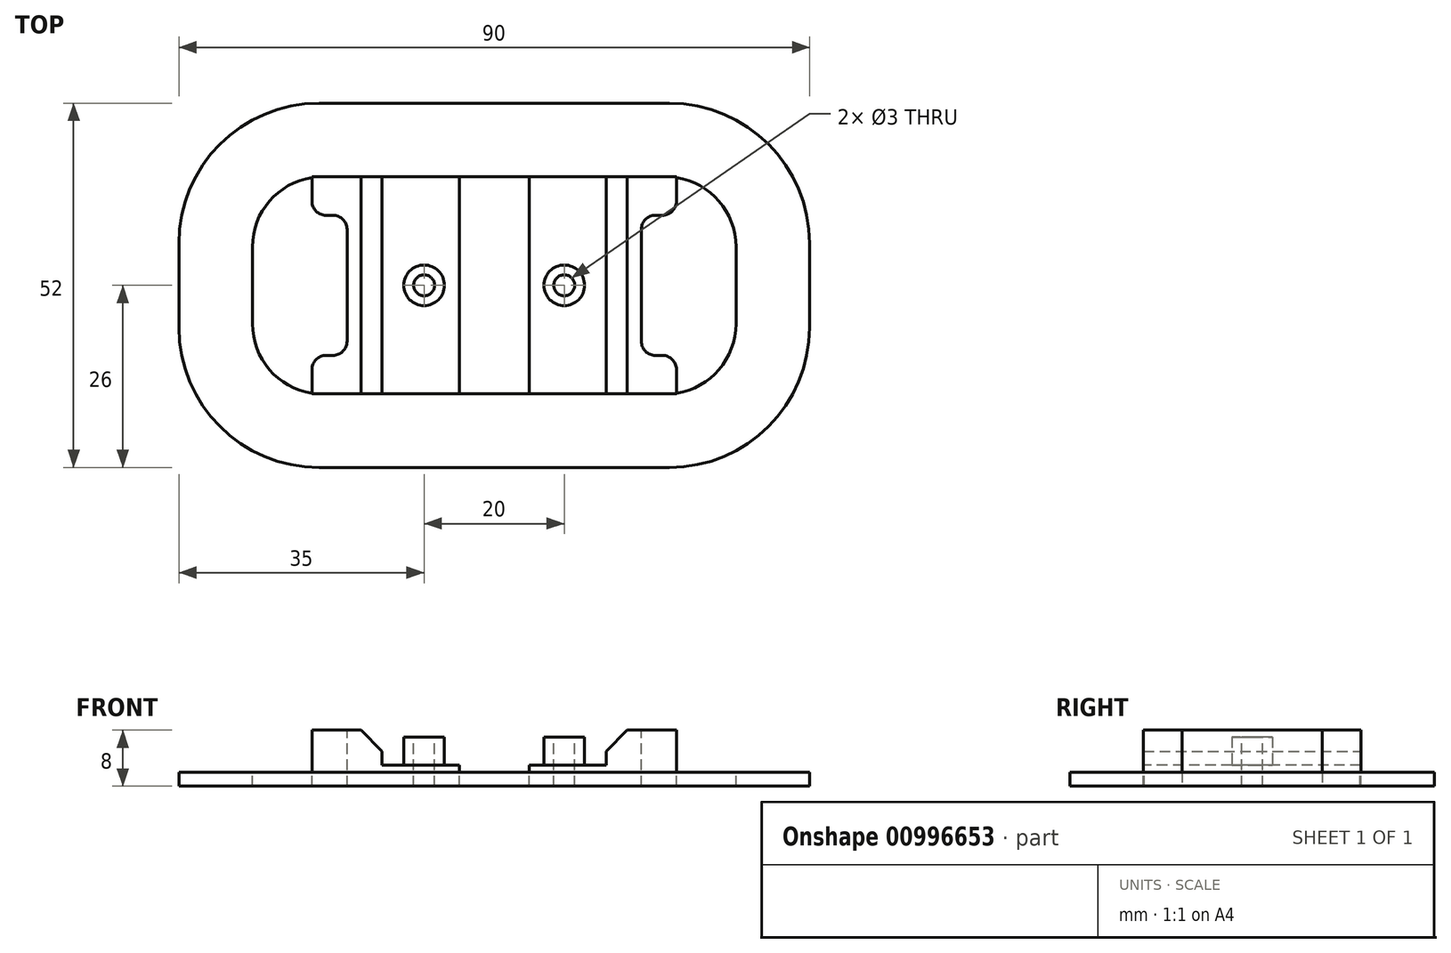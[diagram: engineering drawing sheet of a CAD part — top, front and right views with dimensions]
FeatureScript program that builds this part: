
annotation { "Feature Type Name" : "Feature", "Feature Type Description" : "" }
export const myFeature = defineFeature(function(context is Context, id is Id, definition is map)
    precondition{}
    {
        {
            var Q0;
            Q0=qCreatedBy(makeId("Top.planeOp"),FACE);
            var sketch = newSketch(context, id + "F0", { "sketchPlane" : qUnion([Q0])});
            skLineSegment(sketch, "E0.bottom", {"start": v(26, 15.5) * mm, "end": v(-26, 15.5) * mm});
            skLineSegment(sketch, "E0.top", {"start": v(26, -15.5) * mm, "end": v(-26, -15.5) * mm});
            skLineSegment(sketch, "E0.left", {"start": v(26, 15.5) * mm, "end": v(26, -15.5) * mm});
            skLineSegment(sketch, "E0.right", {"start": v(-26, 15.5) * mm, "end": v(-26, -15.5) * mm});
            skPoint(sketch, "E0.middle", {"position": v(0, 0) * mm});
            skSolve(sketch);
        }
        {
            var Q0;
            Q0 = qSketchRegion(id + "F0", true);
            extrude(context, id + "F1", {"entities" : qUnion([Q0]), "oppositeDirection" : true, "depth" : 3 * mm, "offsetDistance" : 25 * mm});
        }
        {
            var Q0;
            Q0=makeQuery(id+"F1.opExtrude","CAP_FACE",FACE,{"disambiguationData":[OSD([sQuery(id+"F0.wireOp",EDGE,"E0.bottom"),sQuery(id+"F0.wireOp",EDGE,"E0.top"),sQuery(id+"F0.wireOp",EDGE,"E0.left"),sQuery(id+"F0.wireOp",EDGE,"E0.right")])],"isStart":true});
            var sketch = newSketch(context, id + "F2", { "sketchPlane" : qUnion([Q0])});
            skLineSegment(sketch, "E1.bottom", {"start": v(16, -15.5) * mm, "end": v(-16, -15.5) * mm, "construction": true});
            skLineSegment(sketch, "E1.top", {"start": v(16, 15.5) * mm, "end": v(-16, 15.5) * mm, "construction": true});
            skLineSegment(sketch, "E1.left", {"start": v(16, -15.5) * mm, "end": v(16, 15.5) * mm});
            skLineSegment(sketch, "E1.right", {"start": v(-16, -15.5) * mm, "end": v(-16, 15.5) * mm, "construction": true});
            skPoint(sketch, "E1.middle", {"position": v(0, 0) * mm});
            skLineSegment(sketch, "E2.bottom", {"start": v(-16, -15.5) * mm, "end": v(-26, -15.5) * mm});
            skLineSegment(sketch, "E2.top", {"start": v(-16, 15.5) * mm, "end": v(-26, 15.5) * mm});
            skLineSegment(sketch, "E2.left", {"start": v(-16, -15.5) * mm, "end": v(-16, 15.5) * mm});
            skLineSegment(sketch, "E2.right", {"start": v(-26, -15.5) * mm, "end": v(-26, 15.5) * mm});
            skLineSegment(sketch, "E3.bottom", {"start": v(16, -15.5) * mm, "end": v(26, -15.5) * mm});
            skLineSegment(sketch, "E3.top", {"start": v(16, 15.5) * mm, "end": v(26, 15.5) * mm});
            skLineSegment(sketch, "E3.left", {"start": v(16, -15.5) * mm, "end": v(16, 15.5) * mm, "construction": true});
            skLineSegment(sketch, "E3.right", {"start": v(26, -15.5) * mm, "end": v(26, 15.5) * mm});
            skSolve(sketch);
        }
        {
            var Q0;
            Q0 = qSketchRegion(id + "F2", true);
            extrude(context, id + "F3", {"entities" : qUnion([Q0]), "operationType" : NewBodyOperationType.ADD, "depth" : 5 * mm, "offsetDistance" : 25 * mm});
        }
        {
            var Q0;
            Q0=makeQuery(id+"F3.opExtrude","CAP_EDGE",EDGE,{"disambiguationData":[OSD([sQuery(id+"F2.wireOp",EDGE,"E2.left")])],"isStart":false});
            var Q1;
            Q1=makeQuery(id+"F3.opExtrude","CAP_EDGE",EDGE,{"disambiguationData":[OSD([sQuery(id+"F2.wireOp",EDGE,"E1.left")])],"isStart":false});
            chamfer(context, id + "F4", {"entities" : qUnion([Q0, Q1]), "width" : 3 * mm, "tangentPropagation" : true});
        }
        {
            var Q0;
            Q0=makeQuery(id+"F1.opExtrude","CAP_FACE",FACE,{"disambiguationData":[OSD([sQuery(id+"F0.wireOp",EDGE,"E0.bottom"),sQuery(id+"F0.wireOp",EDGE,"E0.top"),sQuery(id+"F0.wireOp",EDGE,"E0.left"),sQuery(id+"F0.wireOp",EDGE,"E0.right")])],"isStart":true});
            var sketch = newSketch(context, id + "F5", { "sketchPlane" : qUnion([Q0])});
            skLineSegment(sketch, "E4", {"start": v(0, -15.5) * mm, "end": v(0, 15.5) * mm, "construction": true});
            skLineSegment(sketch, "E5", {"start": v(-16, 0) * mm, "end": v(16, 0) * mm, "construction": true});
            skCircle(sketch, "E6", {"center": v(-10, 0) * mm, "radius": 2.9 * mm});
            skCircle(sketch, "E7", {"center": v(10, 0) * mm, "radius": 2.9 * mm});
            skSolve(sketch);
        }
        {
            var Q0;
            Q0 = qSketchRegion(id + "F5", true);
            extrude(context, id + "F6", {"entities" : qUnion([Q0]), "operationType" : NewBodyOperationType.ADD, "depth" : 4 * mm, "offsetDistance" : 25 * mm});
        }
        {
            var Q0;
            Q0=makeQuery(id+"F1.opExtrude","CAP_FACE",FACE,{"disambiguationData":[OSD([sQuery(id+"F0.wireOp",EDGE,"E0.bottom"),sQuery(id+"F0.wireOp",EDGE,"E0.top"),sQuery(id+"F0.wireOp",EDGE,"E0.left"),sQuery(id+"F0.wireOp",EDGE,"E0.right")])],"isStart":false});
            var sketch = newSketch(context, id + "F7", { "sketchPlane" : qUnion([Q0])});
            skLineSegment(sketch, "E8.bottom", {"start": v(45, 26) * mm, "end": v(-45, 26) * mm});
            skLineSegment(sketch, "E8.top", {"start": v(45, -26) * mm, "end": v(-45, -26) * mm});
            skLineSegment(sketch, "E8.left", {"start": v(45, 26) * mm, "end": v(45, -26) * mm});
            skLineSegment(sketch, "E8.right", {"start": v(-45, 26) * mm, "end": v(-45, -26) * mm});
            skPoint(sketch, "E8.middle", {"position": v(0, 0) * mm});
            skSolve(sketch);
        }
        {
            var Q0;
            Q0 = qSketchRegion(id + "F7", true);
            extrude(context, id + "F8", {"entities" : qUnion([Q0]), "operationType" : NewBodyOperationType.ADD, "depth" : 2 * mm, "offsetDistance" : 25 * mm, "hasSecondDirection" : true, "secondDirectionOppositeDirection" : true, "secondDirectionDepth" : 1 * mm});
        }
        {
            var Q0;
            Q0=makeQuery(id+"F8.opExtrude","CAP_FACE",FACE,{"disambiguationData":[OSD([sQuery(id+"F7.wireOp",EDGE,"E8.bottom"),sQuery(id+"F7.wireOp",EDGE,"E8.top"),sQuery(id+"F7.wireOp",EDGE,"E8.left"),sQuery(id+"F7.wireOp",EDGE,"E8.right")])],"isStart":true});
            extrude(context, id + "F9", {"entities" : qUnion([Q0]), "operationType" : NewBodyOperationType.ADD, "depth" : 1 * mm, "offsetDistance" : 25 * mm});
        }
        {
            var Q0;
            Q0=makeQuery(id+"F8.opExtrude","CAP_FACE",FACE,{"disambiguationData":[OSD([sQuery(id+"F7.wireOp",EDGE,"E8.bottom"),sQuery(id+"F7.wireOp",EDGE,"E8.top"),sQuery(id+"F7.wireOp",EDGE,"E8.left"),sQuery(id+"F7.wireOp",EDGE,"E8.right")])],"isStart":false});
            extrude(context, id + "F10", {"entities" : qUnion([Q0]), "operationType" : NewBodyOperationType.REMOVE, "oppositeDirection" : true, "depth" : 2 * mm, "offsetDistance" : 25 * mm});
        }
        {
            var Q0;
            {var subQ0=sQuery(id+"F7.wireOp",EDGE,"E8.left");var subQ1=sQuery(id+"F7.wireOp",EDGE,"E8.top");Q0=makeQuery(id+"F9.boolean.opBoolean","MERGE",EDGE,{"derivedFrom":[makeQuery(id+"F8.opExtrude","SWEPT_EDGE",EDGE,{"disambiguationData":[OSD([subQ1,subQ0])]}),makeQuery(id+"F9.opExtrude","SWEPT_EDGE",EDGE,{"disambiguationData":[OSD([subQ1,subQ0])]})]});}
            var Q1;
            {var subQ0=sQuery(id+"F7.wireOp",EDGE,"E8.right");var subQ1=sQuery(id+"F7.wireOp",EDGE,"E8.top");Q1=makeQuery(id+"F9.boolean.opBoolean","MERGE",EDGE,{"derivedFrom":[makeQuery(id+"F8.opExtrude","SWEPT_EDGE",EDGE,{"disambiguationData":[OSD([subQ1,subQ0])]}),makeQuery(id+"F9.opExtrude","SWEPT_EDGE",EDGE,{"disambiguationData":[OSD([subQ1,subQ0])]})]});}
            var Q2;
            {var subQ0=sQuery(id+"F7.wireOp",EDGE,"E8.right");var subQ1=sQuery(id+"F7.wireOp",EDGE,"E8.bottom");Q2=makeQuery(id+"F9.boolean.opBoolean","MERGE",EDGE,{"derivedFrom":[makeQuery(id+"F8.opExtrude","SWEPT_EDGE",EDGE,{"disambiguationData":[OSD([subQ1,subQ0])]}),makeQuery(id+"F9.opExtrude","SWEPT_EDGE",EDGE,{"disambiguationData":[OSD([subQ1,subQ0])]})]});}
            var Q3;
            {var subQ0=sQuery(id+"F7.wireOp",EDGE,"E8.left");var subQ1=sQuery(id+"F7.wireOp",EDGE,"E8.bottom");Q3=makeQuery(id+"F9.boolean.opBoolean","MERGE",EDGE,{"derivedFrom":[makeQuery(id+"F8.opExtrude","SWEPT_EDGE",EDGE,{"disambiguationData":[OSD([subQ1,subQ0])]}),makeQuery(id+"F9.opExtrude","SWEPT_EDGE",EDGE,{"disambiguationData":[OSD([subQ1,subQ0])]})]});}
            fillet(context, id + "F11", {"entities" : qUnion([Q0, Q1, Q2, Q3]), "radius" : 20 * mm, "tangentPropagation" : true, "allowEdgeOverflow" : false});
        }
        {
            var Q0;
            Q0=makeQuery(id+"F6.opExtrude","CAP_FACE",FACE,{"disambiguationData":[OSD([sQuery(id+"F5.wireOp",EDGE,"E6")])],"isStart":false});
            var sketch = newSketch(context, id + "F12", { "sketchPlane" : qUnion([Q0])});
            skCircle(sketch, "E9", {"center": v(-10, 0) * mm, "radius": 1.5 * mm});
            skSolve(sketch);
        }
        {
            var Q0;
            Q0 = qSketchRegion(id + "F12", true);
            extrude(context, id + "F13", {"entities" : qUnion([Q0]), "operationType" : NewBodyOperationType.REMOVE, "oppositeDirection" : true, "depth" : 25 * mm, "offsetDistance" : 25 * mm});
        }
        {
            var Q0;
            Q0=makeQuery(id+"F6.opExtrude","CAP_FACE",FACE,{"disambiguationData":[OSD([sQuery(id+"F5.wireOp",EDGE,"E7")])],"isStart":false});
            var sketch = newSketch(context, id + "F14", { "sketchPlane" : qUnion([Q0])});
            skCircle(sketch, "E10", {"center": v(10, 0) * mm, "radius": 1.5 * mm});
            skSolve(sketch);
        }
        {
            var Q0;
            Q0 = qSketchRegion(id + "F14", true);
            extrude(context, id + "F15", {"entities" : qUnion([Q0]), "operationType" : NewBodyOperationType.REMOVE, "oppositeDirection" : true, "depth" : 25 * mm, "offsetDistance" : 25 * mm});
        }
        {
            var Q0;
            Q0=makeQuery(id+"F9.opExtrude","CAP_FACE",FACE,{"disambiguationData":[OSD([sQuery(id+"F7.wireOp",EDGE,"E8.bottom"),sQuery(id+"F7.wireOp",EDGE,"E8.top"),sQuery(id+"F7.wireOp",EDGE,"E8.left"),sQuery(id+"F7.wireOp",EDGE,"E8.right")])],"isStart":false});
            var sketch = newSketch(context, id + "F16", { "sketchPlane" : qUnion([Q0])});
            skLineSegment(sketch, "E11.bottom", {"start": v(24.5, -15.5) * mm, "end": v(26, -15.5) * mm});
            skLineSegment(sketch, "E11.top", {"start": v(24.5, 15.5) * mm, "end": v(26, 15.5) * mm});
            skLineSegment(sketch, "E11.left", {"start": v(26, -15.5) * mm, "end": v(26, 15.5) * mm});
            skLineSegment(sketch, "E11.right", {"start": v(34.5, -5.5) * mm, "end": v(34.5, 5.5) * mm});
            skPoint(sketch, "E12.visualSharp", {"position": v(34.5, 15.5) * mm});
            skArc(sketch, "E12.filletArc", {"start": v(34.5, 5.5) * mm, "mid": v(32.08, 12.02) * mm, "end": v(26, 15.39) * mm});
            skPoint(sketch, "E13.visualSharp", {"position": v(34.5, -15.5) * mm});
            skArc(sketch, "E13.filletArc", {"start": v(26, -15.39) * mm, "mid": v(32.08, -12.02) * mm, "end": v(34.5, -5.5) * mm});
            skLineSegment(sketch, "E14", {"start": v(0, 0) * mm, "end": v(0, 26) * mm, "construction": true});
            skLineSegment(sketch, "E15.MirrorCS", {"start": v(-24.5, 15.5) * mm, "end": v(-26, 15.5) * mm});
            skLineSegment(sketch, "E16.MirrorCS", {"start": v(-24.5, -15.5) * mm, "end": v(-26, -15.5) * mm});
            skPoint(sketch, "E17.MirrorP", {"position": v(-34.5, -15.5) * mm});
            skLineSegment(sketch, "E18.MirrorCS", {"start": v(-26, -15.5) * mm, "end": v(-26, 15.5) * mm});
            skArc(sketch, "E19.MirrorCS", {"start": v(-26, -15.39) * mm, "mid": v(-32.08, -12.02) * mm, "end": v(-34.5, -5.5) * mm});
            skPoint(sketch, "E20.MirrorP", {"position": v(-34.5, 15.5) * mm});
            skLineSegment(sketch, "E21.MirrorCS", {"start": v(-34.5, -5.5) * mm, "end": v(-34.5, 5.5) * mm});
            skArc(sketch, "E22.MirrorCS", {"start": v(-34.5, 5.5) * mm, "mid": v(-32.08, 12.02) * mm, "end": v(-26, 15.39) * mm});
            skSolve(sketch);
        }
        {
            var Q0;
            Q0 = qSketchRegion(id + "F16", true);
            extrude(context, id + "F17", {"entities" : qUnion([Q0]), "operationType" : NewBodyOperationType.REMOVE, "oppositeDirection" : true, "depth" : 25 * mm, "offsetDistance" : 25 * mm});
        }
        {
            var Q0;
            Q0=makeQuery(id+"F1.opExtrude","CAP_FACE",FACE,{"disambiguationData":[OSD([sQuery(id+"F0.wireOp",EDGE,"E0.bottom"),sQuery(id+"F0.wireOp",EDGE,"E0.top"),sQuery(id+"F0.wireOp",EDGE,"E0.left"),sQuery(id+"F0.wireOp",EDGE,"E0.right")])],"isStart":true});
            var sketch = newSketch(context, id + "F18", { "sketchPlane" : qUnion([Q0])});
            skLineSegment(sketch, "E23.bottom", {"start": v(-5, 15.5) * mm, "end": v(5, 15.5) * mm});
            skLineSegment(sketch, "E23.top", {"start": v(-5, -15.5) * mm, "end": v(5, -15.5) * mm});
            skLineSegment(sketch, "E23.left", {"start": v(-5, 15.5) * mm, "end": v(-5, -15.5) * mm});
            skLineSegment(sketch, "E23.right", {"start": v(5, 15.5) * mm, "end": v(5, -15.5) * mm});
            skPoint(sketch, "E23.middle", {"position": v(0, 0) * mm});
            skSolve(sketch);
        }
        {
            var Q0;
            Q0 = qSketchRegion(id + "F18", true);
            extrude(context, id + "F19", {"entities" : qUnion([Q0]), "operationType" : NewBodyOperationType.REMOVE, "oppositeDirection" : true, "depth" : 25 * mm, "offsetDistance" : 25 * mm});
        }
        {
            var Q0;
            Q0=makeQuery(id+"F3.opExtrude","CAP_FACE",FACE,{"disambiguationData":[OSD([sQuery(id+"F2.wireOp",EDGE,"E1.left"),sQuery(id+"F2.wireOp",EDGE,"E3.bottom"),sQuery(id+"F2.wireOp",EDGE,"E3.top"),sQuery(id+"F2.wireOp",EDGE,"E3.right")])],"isStart":false});
            var sketch = newSketch(context, id + "F20", { "sketchPlane" : qUnion([Q0])});
            skLineSegment(sketch, "E24.bottom", {"start": v(31, 10) * mm, "end": v(21, 10) * mm});
            skLineSegment(sketch, "E24.top", {"start": v(31, -10) * mm, "end": v(21, -10) * mm});
            skLineSegment(sketch, "E24.left", {"start": v(31, 10) * mm, "end": v(31, -10) * mm});
            skLineSegment(sketch, "E24.right", {"start": v(21, 10) * mm, "end": v(21, -10) * mm});
            skPoint(sketch, "E24.middle", {"position": v(26, 0) * mm});
            skSolve(sketch);
        }
        {
            var Q0;
            Q0 = qSketchRegion(id + "F20", true);
            extrude(context, id + "F21", {"entities" : qUnion([Q0]), "operationType" : NewBodyOperationType.REMOVE, "oppositeDirection" : true, "depth" : 25 * mm, "offsetDistance" : 25 * mm});
        }
        {
            var Q0;
            Q0=makeQuery(id+"F3.opExtrude","CAP_FACE",FACE,{"disambiguationData":[OSD([sQuery(id+"F2.wireOp",EDGE,"E2.bottom"),sQuery(id+"F2.wireOp",EDGE,"E2.top"),sQuery(id+"F2.wireOp",EDGE,"E2.left"),sQuery(id+"F2.wireOp",EDGE,"E2.right")])],"isStart":false});
            var sketch = newSketch(context, id + "F22", { "sketchPlane" : qUnion([Q0])});
            skLineSegment(sketch, "E25.bottom", {"start": v(-21, 10) * mm, "end": v(-31, 10) * mm});
            skLineSegment(sketch, "E25.top", {"start": v(-21, -10) * mm, "end": v(-31, -10) * mm});
            skLineSegment(sketch, "E25.left", {"start": v(-21, 10) * mm, "end": v(-21, -10) * mm});
            skLineSegment(sketch, "E25.right", {"start": v(-31, 10) * mm, "end": v(-31, -10) * mm});
            skPoint(sketch, "E25.middle", {"position": v(-26, 0) * mm});
            skSolve(sketch);
        }
        {
            var Q0;
            Q0 = qSketchRegion(id + "F22", true);
            extrude(context, id + "F23", {"entities" : qUnion([Q0]), "operationType" : NewBodyOperationType.REMOVE, "oppositeDirection" : true, "depth" : 25 * mm, "offsetDistance" : 25 * mm});
        }
        {
            var Q0;
            Q0=makeQuery(id+"F21.boolean.opBoolean","COPY",EDGE,{"derivedFrom":makeQuery(id+"F21.opExtrude","SWEPT_EDGE",EDGE,{"disambiguationData":[OSD([sQuery(id+"F20.wireOp",EDGE,"E24.bottom"),sQuery(id+"F20.wireOp",EDGE,"E24.right")])]})});
            var Q1;
            Q1=makeQuery(id+"F21.boolean.opBoolean","COPY",EDGE,{"derivedFrom":makeQuery(id+"F21.opExtrude","SWEPT_EDGE",EDGE,{"disambiguationData":[OSD([sQuery(id+"F20.wireOp",EDGE,"E24.top"),sQuery(id+"F20.wireOp",EDGE,"E24.right")])]})});
            var Q2;
            Q2=makeQuery(id+"F23.boolean.opBoolean","COPY",EDGE,{"derivedFrom":makeQuery(id+"F23.opExtrude","SWEPT_EDGE",EDGE,{"disambiguationData":[OSD([sQuery(id+"F22.wireOp",EDGE,"E25.bottom"),sQuery(id+"F22.wireOp",EDGE,"E25.left")])]})});
            var Q3;
            Q3=makeQuery(id+"F23.boolean.opBoolean","COPY",EDGE,{"derivedFrom":makeQuery(id+"F23.opExtrude","SWEPT_EDGE",EDGE,{"disambiguationData":[OSD([sQuery(id+"F22.wireOp",EDGE,"E25.top"),sQuery(id+"F22.wireOp",EDGE,"E25.left")])]})});
            var Q4;
            Q4=makeQuery(id+"F23.boolean.opBoolean","INTERSECT",EDGE,{"derivedFrom":[makeQuery(id+"F17.boolean.opBoolean","MERGE",FACE,{"derivedFrom":[makeQuery(id+"F3.boolean.opBoolean","MERGE",FACE,{"derivedFrom":[makeQuery(id+"F1.opExtrude","SWEPT_FACE",FACE,{"disambiguationData":[OSD([sQuery(id+"F0.wireOp",EDGE,"E0.right")])]}),makeQuery(id+"F3.opExtrude","SWEPT_FACE",FACE,{"disambiguationData":[OSD([sQuery(id+"F2.wireOp",EDGE,"E2.right")])]})]})],"fromTools":[makeQuery(id+"F17.opExtrude","SWEPT_FACE",FACE,{"disambiguationData":[OSD([sQuery(id+"F16.wireOp",EDGE,"E18.MirrorCS")])]})]}),makeQuery(id+"F23.opExtrude","SWEPT_FACE",FACE,{"disambiguationData":[OSD([sQuery(id+"F22.wireOp",EDGE,"E25.top")])]})]});
            var Q5;
            Q5=makeQuery(id+"F23.boolean.opBoolean","INTERSECT",EDGE,{"derivedFrom":[makeQuery(id+"F17.boolean.opBoolean","MERGE",FACE,{"derivedFrom":[makeQuery(id+"F3.boolean.opBoolean","MERGE",FACE,{"derivedFrom":[makeQuery(id+"F1.opExtrude","SWEPT_FACE",FACE,{"disambiguationData":[OSD([sQuery(id+"F0.wireOp",EDGE,"E0.right")])]}),makeQuery(id+"F3.opExtrude","SWEPT_FACE",FACE,{"disambiguationData":[OSD([sQuery(id+"F2.wireOp",EDGE,"E2.right")])]})]})],"fromTools":[makeQuery(id+"F17.opExtrude","SWEPT_FACE",FACE,{"disambiguationData":[OSD([sQuery(id+"F16.wireOp",EDGE,"E18.MirrorCS")])]})]}),makeQuery(id+"F23.opExtrude","SWEPT_FACE",FACE,{"disambiguationData":[OSD([sQuery(id+"F22.wireOp",EDGE,"E25.bottom")])]})]});
            var Q6;
            Q6=makeQuery(id+"F21.boolean.opBoolean","INTERSECT",EDGE,{"derivedFrom":[makeQuery(id+"F17.boolean.opBoolean","MERGE",FACE,{"derivedFrom":[makeQuery(id+"F3.boolean.opBoolean","MERGE",FACE,{"derivedFrom":[makeQuery(id+"F1.opExtrude","SWEPT_FACE",FACE,{"disambiguationData":[OSD([sQuery(id+"F0.wireOp",EDGE,"E0.left")])]}),makeQuery(id+"F3.opExtrude","SWEPT_FACE",FACE,{"disambiguationData":[OSD([sQuery(id+"F2.wireOp",EDGE,"E3.right")])]})]})],"fromTools":[makeQuery(id+"F17.opExtrude","SWEPT_FACE",FACE,{"disambiguationData":[OSD([sQuery(id+"F16.wireOp",EDGE,"E11.left")])]})]}),makeQuery(id+"F21.opExtrude","SWEPT_FACE",FACE,{"disambiguationData":[OSD([sQuery(id+"F20.wireOp",EDGE,"E24.bottom")])]})]});
            var Q7;
            Q7=makeQuery(id+"F21.boolean.opBoolean","INTERSECT",EDGE,{"derivedFrom":[makeQuery(id+"F17.boolean.opBoolean","MERGE",FACE,{"derivedFrom":[makeQuery(id+"F3.boolean.opBoolean","MERGE",FACE,{"derivedFrom":[makeQuery(id+"F1.opExtrude","SWEPT_FACE",FACE,{"disambiguationData":[OSD([sQuery(id+"F0.wireOp",EDGE,"E0.left")])]}),makeQuery(id+"F3.opExtrude","SWEPT_FACE",FACE,{"disambiguationData":[OSD([sQuery(id+"F2.wireOp",EDGE,"E3.right")])]})]})],"fromTools":[makeQuery(id+"F17.opExtrude","SWEPT_FACE",FACE,{"disambiguationData":[OSD([sQuery(id+"F16.wireOp",EDGE,"E11.left")])]})]}),makeQuery(id+"F21.opExtrude","SWEPT_FACE",FACE,{"disambiguationData":[OSD([sQuery(id+"F20.wireOp",EDGE,"E24.top")])]})]});
            fillet(context, id + "F24", {"entities" : qUnion([Q0, Q1, Q2, Q3, Q4, Q5, Q6, Q7]), "radius" : 2 * mm, "tangentPropagation" : true, "allowEdgeOverflow" : false});
        }
    });
